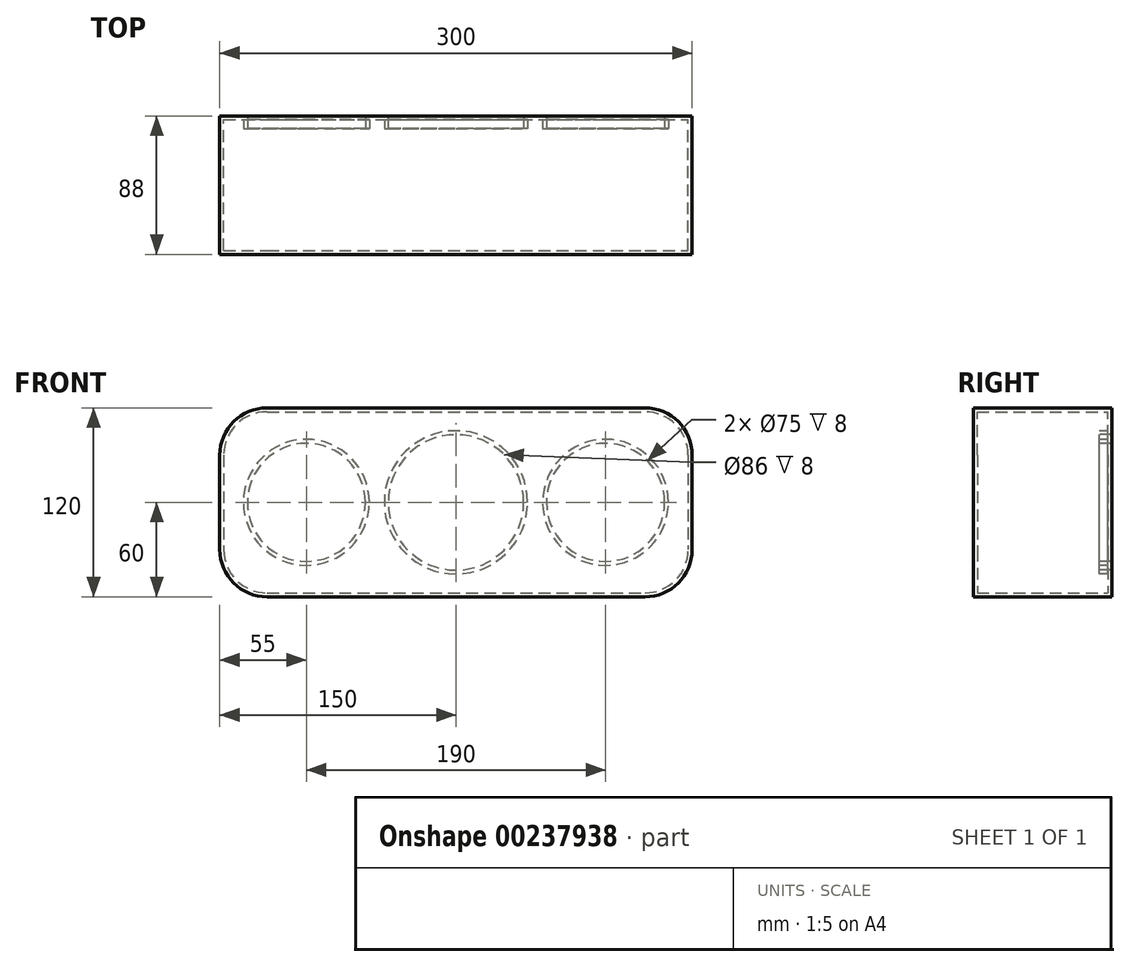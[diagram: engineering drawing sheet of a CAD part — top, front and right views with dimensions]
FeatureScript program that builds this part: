
annotation { "Feature Type Name" : "Feature", "Feature Type Description" : "" }
export const myFeature = defineFeature(function(context is Context, id is Id, definition is map)
    precondition{}
    {
        {
            var Q0;
            Q0=qCreatedBy(makeId("Front.planeOp"),FACE);
            var sketch = newSketch(context, id + "F0", { "sketchPlane" : qUnion([Q0])});
            skLineSegment(sketch, "E0.bottom", {"start": v(-120, 60) * mm, "end": v(120, 60) * mm});
            skLineSegment(sketch, "E0.top", {"start": v(-120, -60) * mm, "end": v(120, -60) * mm});
            skLineSegment(sketch, "E0.left", {"start": v(-150, 30) * mm, "end": v(-150, -30) * mm});
            skLineSegment(sketch, "E0.right", {"start": v(150, 30) * mm, "end": v(150, -30) * mm});
            skPoint(sketch, "E0.middle", {"position": v(0, 0) * mm});
            skPoint(sketch, "E1.visualSharp", {"position": v(-150, 60) * mm});
            skArc(sketch, "E1.filletArc", {"start": v(-120, 60) * mm, "mid": v(-141.21, 51.21) * mm, "end": v(-150, 30) * mm});
            skPoint(sketch, "E2.visualSharp", {"position": v(-150, -60) * mm});
            skArc(sketch, "E2.filletArc", {"start": v(-150, -30) * mm, "mid": v(-141.21, -51.21) * mm, "end": v(-120, -60) * mm});
            skPoint(sketch, "E3.visualSharp", {"position": v(150, -60) * mm});
            skArc(sketch, "E3.filletArc", {"start": v(120, -60) * mm, "mid": v(141.21, -51.21) * mm, "end": v(150, -30) * mm});
            skPoint(sketch, "E4.visualSharp", {"position": v(150, 60) * mm});
            skArc(sketch, "E4.filletArc", {"start": v(150, 30) * mm, "mid": v(141.21, 51.21) * mm, "end": v(120, 60) * mm});
            skSolve(sketch);
        }
        {
            var Q0;
            Q0=makeQuery(id+"F0.imprint","IMPRINT",FACE,{"disambiguationData":[TD([[makeQuery(id+"F0.imprint","IMPRINT",EDGE,{"derivedFrom":sQuery(id+"F0.wireOp",EDGE,"E0.bottom")}),-1.0]])]});
            extrude(context, id + "F1", {"entities" : qUnion([Q0]), "depth" : 80 * mm});
        }
        {
            var Q0;
            Q0=qCreatedBy(makeId("Front.planeOp"),FACE);
            var sketch = newSketch(context, id + "F2", { "sketchPlane" : qUnion([Q0])});
            skLineSegment(sketch, "E5.bottom", {"start": v(-120, 60) * mm, "end": v(120, 60) * mm});
            skLineSegment(sketch, "E5.top", {"start": v(-120, -60) * mm, "end": v(120, -60) * mm});
            skLineSegment(sketch, "E5.left", {"start": v(-150, 30) * mm, "end": v(-150, -30) * mm});
            skLineSegment(sketch, "E5.right", {"start": v(150, 30) * mm, "end": v(150, -30) * mm});
            skPoint(sketch, "E5.middle", {"position": v(0, 0) * mm});
            skPoint(sketch, "E6.visualSharp", {"position": v(-150, 60) * mm});
            skArc(sketch, "E6.filletArc", {"start": v(-120, 60) * mm, "mid": v(-141.21, 51.21) * mm, "end": v(-150, 30) * mm});
            skPoint(sketch, "E7.visualSharp", {"position": v(-150, -60) * mm});
            skArc(sketch, "E7.filletArc", {"start": v(-150, -30) * mm, "mid": v(-141.21, -51.21) * mm, "end": v(-120, -60) * mm});
            skPoint(sketch, "E8.visualSharp", {"position": v(150, -60) * mm});
            skArc(sketch, "E8.filletArc", {"start": v(120, -60) * mm, "mid": v(141.21, -51.21) * mm, "end": v(150, -30) * mm});
            skPoint(sketch, "E9.visualSharp", {"position": v(150, 60) * mm});
            skArc(sketch, "E9.filletArc", {"start": v(150, 30) * mm, "mid": v(141.21, 51.21) * mm, "end": v(120, 60) * mm});
            skCircle(sketch, "E10", {"center": v(0, 0) * mm, "radius": 47.5 * mm, "construction": true});
            skCircle(sketch, "E11", {"center": v(0, 0) * mm, "radius": 43 * mm});
            skCircle(sketch, "E12", {"center": v(-95, 0) * mm, "radius": 37.5 * mm});
            skCircle(sketch, "E13.MirrorC", {"center": v(95, 0) * mm, "radius": 37.5 * mm});
            skSolve(sketch);
        }
        {
            var Q0;
            Q0=makeQuery(id+"F2.imprint","IMPRINT",FACE,{"disambiguationData":[TD([[makeQuery(id+"F2.imprint","IMPRINT",EDGE,{"derivedFrom":sQuery(id+"F2.wireOp",EDGE,"E5.bottom")}),-1.0]])]});
            extrude(context, id + "F3", {"entities" : qUnion([Q0]), "operationType" : NewBodyOperationType.ADD, "oppositeDirection" : true, "depth" : 8 * mm});
        }
        {
            var Q0;
            Q0=makeQuery(id+"F1.opExtrude","CAP_FACE",FACE,{"disambiguationData":[OSD([sQuery(id+"F0.wireOp",EDGE,"E0.bottom"),sQuery(id+"F0.wireOp",EDGE,"E0.top"),sQuery(id+"F0.wireOp",EDGE,"E0.left"),sQuery(id+"F0.wireOp",EDGE,"E0.right"),sQuery(id+"F0.wireOp",EDGE,"E1.filletArc"),sQuery(id+"F0.wireOp",EDGE,"E2.filletArc"),sQuery(id+"F0.wireOp",EDGE,"E3.filletArc"),sQuery(id+"F0.wireOp",EDGE,"E4.filletArc")])],"isStart":true});
            shell(context, id + "F4", {"entities" : qUnion([Q0]), "thickness" : 2.5 * mm});
        }
    });
